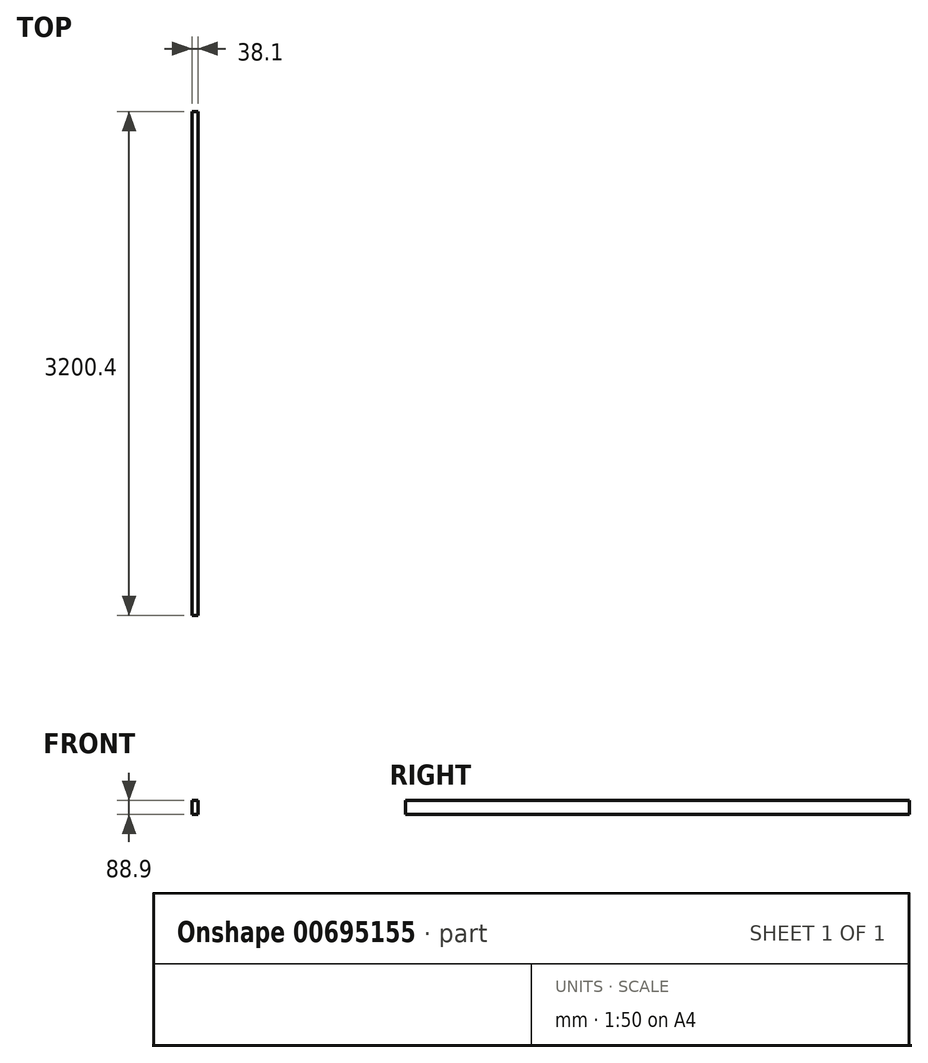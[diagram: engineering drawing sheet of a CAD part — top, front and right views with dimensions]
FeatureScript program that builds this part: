
annotation { "Feature Type Name" : "Feature", "Feature Type Description" : "" }
export const myFeature = defineFeature(function(context is Context, id is Id, definition is map)
    precondition{}
    {
        {
            var Q0;
            Q0=qCreatedBy(makeId("Front.planeOp"),FACE);
            var sketch = newSketch(context, id + "F0", { "sketchPlane" : qUnion([Q0])});
            skLineSegment(sketch, "E0.bottom", {"start": v(207.77, 185.7) * mm, "end": v(245.87, 185.7) * mm});
            skLineSegment(sketch, "E0.top", {"start": v(207.77, 96.8) * mm, "end": v(245.87, 96.8) * mm});
            skLineSegment(sketch, "E0.left", {"start": v(207.77, 185.7) * mm, "end": v(207.77, 96.8) * mm});
            skLineSegment(sketch, "E0.right", {"start": v(245.87, 185.7) * mm, "end": v(245.87, 96.8) * mm});
            skSolve(sketch);
        }
        {
            var Q0;
            Q0=makeQuery(id+"F0.imprint","IMPRINT",FACE,{"disambiguationData":[TD([[makeQuery(id+"F0.imprint","IMPRINT",EDGE,{"derivedFrom":sQuery(id+"F0.wireOp",EDGE,"E0.bottom")}),-1.0]])]});
            extrude(context, id + "F1", {"entities" : qUnion([Q0]), "depth" : 3200.4 * mm, "offsetDistance" : 25.4 * mm});
        }
    });
